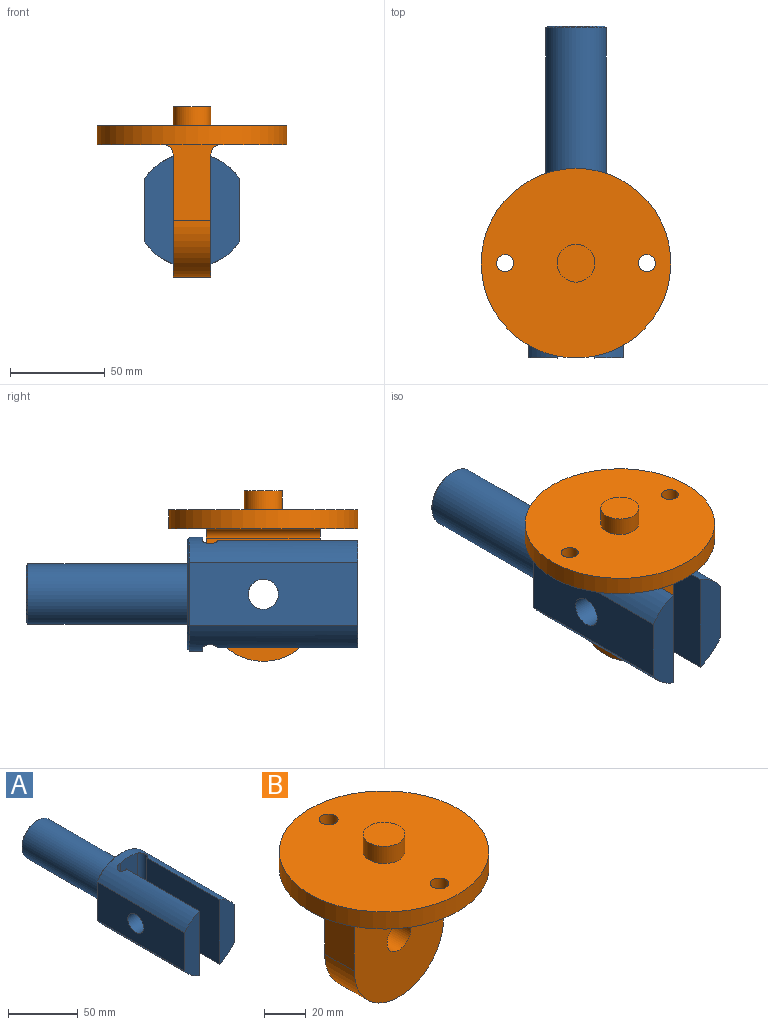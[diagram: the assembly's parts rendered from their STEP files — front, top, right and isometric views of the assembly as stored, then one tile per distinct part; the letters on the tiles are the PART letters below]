
ASSEMBLY  parts=2 mates=1
PART A: 21 faces, bbox 49.8x175x60 mm
  f0: cylinder r=30mm len=89mm, axis (0,1,0), area 3508.4mm2, adj f4,f5,f6,f7,f8,f9,f10,f14
  f1: cylinder r=30mm len=89mm, axis (0,1,0), area 3508.4mm2, adj f4,f5,f6,f7,f8,f9,f10,f15
  f2: plane 58x47.81mm, normal (0,1,0), area 1610.6mm2, adj f11,f13,f14,f15,f16
  f3: cylinder r=8mm len=16mm, axis (1,0,0), area 749.3mm2, adj f6,f9
  f4: plane 60x17.54mm, normal (0,-1,0), area 1037.3mm2, adj f0,f1,f7,f8
  f5: plane 74x56.57mm, normal (-1,0,0), area 3985mm2, adj f0,f1,f8,f18,f19
  f6: plane 74.01x56.57mm, normal (1,0,0), area 3985.3mm2, adj f0,f1,f3,f7,f20
  f7: cylinder r=4mm len=57.46mm, axis (0,0,-1), area 741.6mm2, adj f0,f1,f4,f6
  f8: cylinder r=4mm len=57.3mm, axis (0,0,-1), area 753.2mm2, adj f0,f1,f4,f5
  f9: plane 89x33.45mm, normal (-1,0,0), area 2775.6mm2, adj f0,f1,f3,f16,f20
  f10: plane 89x33.45mm, normal (1,0,0), area 2775.6mm2, adj f0,f1,f13,f18,f19
  f11: cylinder r=16mm len=84mm, axis (0,-1,0), area 8444.6mm2, adj f2,f17
  f12: plane 30x30mm, normal (0,1,0), area 706.9mm2, adj f17
  f13: plane 33.45x1mm, normal (0.71,0.71,0), area 46.9mm2, adj f2,f10,f14,f15
  f14: cone r=30mm half-angle=45deg, axis (0,-1,0), area 81.3mm2, adj f0,f2,f13,f16
  f15: cone r=30mm half-angle=45deg, axis (0,-1,0), area 81.3mm2, adj f1,f2,f13,f16
  f16: plane 33.45x1mm, normal (-0.71,0.71,0), area 46.9mm2, adj f2,f9,f14,f15
  f17: cone r=15mm half-angle=45deg, axis (0,-1,0), area 137.7mm2, adj f11,f12
  f18: cylinder r=8mm len=16mm, axis (-1,0,0), area 749.3mm2, adj f5,f10
  f19: plane 56.57x14.91mm, normal (0,-1,0), area 709.4mm2, adj f0,f1,f5,f10
  f20: plane 56.57x14.91mm, normal (0,-1,0), area 709.4mm2, adj f0,f1,f6,f9
PART B: 15 faces, bbox 100x100x90 mm
  f0: cylinder r=50mm len=100mm, axis (0,0,-1), area 3141.6mm2, adj f1,f2
  f1: plane 100x100mm, normal (0,0,1), area 7412.6mm2, adj f0,f7,f13,f14
  f2: plane 100x100mm, normal (0,0,-1), area 5926.7mm2, adj f0,f3,f5,f11,f12,f13,f14
  f3: plane 40x30mm, normal (1,0,0), area 810.7mm2, adj f2,f4,f6,f10,f11,f12
  f4: plane 65x60mm, normal (0,-1,0), area 3312.7mm2, adj f3,f5,f9,f10,f11
  f5: plane 40x30mm, normal (-1,0,0), area 810.7mm2, adj f2,f4,f6,f10,f11,f12
  f6: plane 65x60mm, normal (0,1,0), area 3312.7mm2, adj f3,f5,f9,f10,f12
  f7: cylinder r=10mm len=20mm, axis (0,0,-1), area 628.3mm2, adj f1,f8
  f8: plane 20x20mm, normal (0,0,1), area 314.2mm2, adj f7
  f9: cylinder r=8mm len=20mm, axis (0,-1,0), area 1005.3mm2, adj f4,f6
  f10: cylinder r=30mm len=60mm, axis (0,1,0), area 1885mm2, adj f3,f4,f5,f6
  f11: cylinder r=5mm len=60mm, axis (1,0,0), area 471.2mm2, adj f2,f3,f4,f5
  f12: cylinder r=5mm len=60mm, axis (-1,0,0), area 471.2mm2, adj f2,f3,f5,f6
  f13: cylinder r=4.5mm len=10mm, axis (0,0,1), area 282.7mm2, adj f1,f2
  f14: cylinder r=4.5mm len=10mm, axis (0,0,1), area 282.7mm2, adj f1,f2
PLACE A at identity
PLACE B rot(axis=(0,0,1),90deg) t=(0,-40.13,34.6)mm
MATE revolute B.f9 <-> A.f3  axis (1,0,0) through (10,-40.13,0)mm
